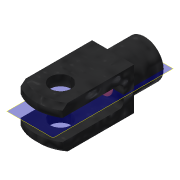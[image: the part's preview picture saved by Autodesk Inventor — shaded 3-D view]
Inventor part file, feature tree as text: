
AUTODESK INVENTOR PART (.ipt)
format: ipt  version: 2016 (Build 200138000, 138)  size: 159,232 bytes
history: native  units: in
note: dims shown in document units (in); Inventor stores cm internally (conversion verified against a paired STEP export)
features: plane x2, other x1
ambient origin geometry x8: Origin, YZ Plane, XZ Plane, XY Plane, X Axis, Y Axis, Z Axis, Center Point
bodies: Solid1 (feature_tree)
feature tree (3):
  other  "GERM_10_F_21"
  plane  "Work Plane1"
  plane  "Work Plane2"
